# Revit family: Haworth_Riverbend_ConcaveBench60_AP_PRELIMINARY
name_source: partatom
category: Furniture
revit_build: Autodesk Revit 2018 (Build: 20170223_1515(x64)
units: mm (PartAtom-declared; Revit-internal decimal feet)

## family parameters
Always vertical = Yes
Cut with Voids When Loaded = No
OmniClass Number = 23.40.70.14.64.21
OmniClass Title = Systems Furniture
Room Calculation Point = No
Shared = No
Work Plane-Based = No

## types (6) — shared parameters
Actual Width = 1430 mm  [stored 4.6916 ft]
Assembly Code = E2020200
Description = Haworth - Riverbend - Concave Bench - 60 Degree
Manufacturer = Haworth
Model = SERICX6F
Revision Number = 1
Size = Verify Final Dim. w/ Haworth
Trim Finish = Haworth _ Paint _ Plaster
URL = https://www.haworth.com
URL - Product = https://www.haworth.com
Warranty = http://www.haworth.com

## per-type parameters (varying)
| type | Actual Depth | Actual Height | High | High Back | Large | Low | Mid Back | No Back | Small | Width Straight Edge |
| 1430w x 930d x 450h - High Back | 930 mm  [stored 3.05118 ft] | 450 mm  [stored 1.47638 ft] | Yes | Yes | Yes | No | No | No | No | 930 mm  [stored 3.05118 ft] |
| 1430w x 930d x 390h - Mid Back | 930 mm  [stored 3.05118 ft] | 390 mm  [stored 1.27953 ft] | No | No | Yes | Yes | Yes | No | No | 930 mm  [stored 3.05118 ft] |
| 1430w x 930d x 390h - No Back | 930 mm  [stored 3.05118 ft] | 390 mm  [stored 1.27953 ft] | No | No | Yes | Yes | No | Yes | No | 930 mm  [stored 3.05118 ft] |
| 1430w x 880d x 390h - High Back | 880 mm  [stored 2.88714 ft] | 390 mm  [stored 1.27953 ft] | No | Yes | No | Yes | No | No | Yes | 880 mm  [stored 2.88714 ft] |
| 1430w x 880d x 450h - Mid Back | 880 mm  [stored 2.88714 ft] | 450 mm  [stored 1.47638 ft] | Yes | No | No | No | Yes | No | Yes | 880 mm  [stored 2.88714 ft] |
| 1430w x 880d x 390h - No Back | 880 mm  [stored 2.88714 ft] | 390 mm  [stored 1.27953 ft] | No | No | No | Yes | No | Yes | Yes | 880 mm  [stored 2.88714 ft] |

note: [stored X ft] marks values corroborated as IEEE doubles in the binary element streams (Revit-internal decimal feet)

## geometry (parser evidence)
native form markers: Sweep x15
no freeform markers — native parametric forms only
